# Revit family: 756-218-005 DN150-600
name_source: partatom
category: Pipe Accessories
units: mm (PartAtom-declared; Revit-internal decimal feet)

## family parameters
Always vertical = Yes
Cut with Voids When Loaded = No
Part Type = Valve - Breaks Into
Round Connector Dimension = Use Diameter
Shared = No
Work Plane-Based = No

## types (17) — shared parameters
1 = 1 mm  [stored 0.00328084 ft]
10 = 10 mm  [stored 0.0328084 ft]
15 = 15 mm  [stored 0.0492126 ft]
2 = 2 mm  [stored 0.00656168 ft]
20 = 20 mm  [stored 0.0656168 ft]
3 = 3 mm  [stored 0.00984252 ft]
40 = 40 mm  [stored 0.131234 ft]
82 = 84 mm
DN150_PN16 = 756-0150-2-14018014
DN200_PN10 = 756-0200-2-04018014
DN200_PN16 = 756-0200-2-14018014
DN250_PN10 = 756-0250-2-04018014
DN250_PN16 = 756-0250-2-14018014
DN300_PN10 = 756-0300-2-04018014
DN300_PN16 = 756-0300-2-14018014
DN350_PN10 = 756-0350-2-04018014
DN350_PN16 = 756-0350-2-14018014
DN400_PN10 = 756-0400-2-04018014
DN400_PN16 = 756-0400-2-14018014
DN450_PN10 = 756-0450-2-04018014
DN450_PN16 = 756-0450-2-14018014
DN500_PN10 = 756-0500-2-04018014
DN500_PN16 = 756-0500-2-14018014
DN600_PN10 = 756-0600-2-04018014
DN600_PN16 = 756-0600-2-14018014
Description_ = AVK DOUBLE ECC. BUTTERFLY VALVE, SHORT, PN10/16
Search_table = 756-218-005 DN150-600
URL_product_page = https://www.avkvalves.com
zero-valued in all types: Default Elevation

## per-type parameters (varying)
- DN150_PN16: Bore=75 mm; D=250 mm; D/2=125 mm; DN=150 mm; Disk_T=6 mm  [stored 0.019685 ft]; Disk_T1=6 mm  [stored 0.019685 ft]; FL_T=19 mm  [stored 0.062336 ft]; Fillet=8 mm  [stored 0.0262467 ft]; Gearbox_Sitting_OD=46 mm; Gearbox_Sitting_shaft=25 mm  [stored 0.082021 ft]; Gearbox_dim1=8 mm  [stored 0.0262467 ft]; Gearbox_od=44 mm; H2=201 mm; H2-H22=111 mm; H22=181 mm; Handwheel_dim2=5 mm  [stored 0.0164042 ft]; Handwheet_shaft=5 mm  [stored 0.0164042 ft]; L=140 mm; L/2=70 mm; L1=1 mm  [stored 0.00328084 ft]; L1+(L/2)=210 mm; L1+L/2=71 mm; L2=7 mm  [stored 0.0229659 ft]; L2+(L/2)=77 mm; Location1=28 mm  [stored 0.0918635 ft]; OD=143 mm; Raised_R=106 mm; Raised_dis=3 mm  [stored 0.00984252 ft]; Rib_H=157 mm; Rib_dim1=64 mm; Rib_dim2=45 mm; Thickness=5 mm  [stored 0.0164042 ft]; W1=155 mm; W11=147 mm; W2=263 mm; W2-W22=26 mm; W22=210 mm; W23=189 mm; W3=17 mm  [stored 0.0557743 ft]; W4=60 mm; W5=276 mm; W55=221 mm; disk_dim1=38 mm; disk_dim2=21 mm  [stored 0.0688976 ft]; disk_dim3=6 mm  [stored 0.019685 ft]; disk_dim4=7 mm  [stored 0.0229659 ft]; dist_Extr=14 mm  [stored 0.0459318 ft]; gearbox_dim2=18 mm  [stored 0.0590551 ft]; handwheel_dim1=3 mm  [stored 0.00984252 ft]; location=21 mm  [stored 0.0688976 ft]; raised_R1=110 mm; shaft_path=120 mm; total_dik_Dia=147 mm
- DN200_PN10: Bore=100 mm; D=250 mm; D/2=125 mm; DN=200 mm; Disk_T=10 mm  [stored 0.0328084 ft]; Disk_T1=6 mm  [stored 0.019685 ft]; FL_T=20 mm  [stored 0.0656168 ft]; Fillet=9 mm  [stored 0.0295276 ft]; Gearbox_Sitting_OD=50 mm; Gearbox_Sitting_shaft=28 mm  [stored 0.0918635 ft]; Gearbox_dim1=9 mm  [stored 0.0295276 ft]; Gearbox_od=48 mm; H2=227 mm; H2-H22=125 mm; H22=204 mm; Handwheel_dim2=6 mm  [stored 0.019685 ft]; Handwheet_shaft=5 mm  [stored 0.0164042 ft]; L=152 mm; L/2=76 mm; L1=15 mm  [stored 0.0492126 ft]; L1+(L/2)=230 mm; L1+L/2=91 mm; L2=25 mm  [stored 0.082021 ft]; L2+(L/2)=101 mm; Location1=31 mm; OD=170 mm; Raised_R=133 mm; Raised_dis=3 mm  [stored 0.00984252 ft]; Rib_H=187 mm; Rib_dim1=77 mm; Rib_dim2=54 mm; Thickness=5 mm  [stored 0.0164042 ft]; W1=182 mm; W11=173 mm; W2=287 mm; W2-W22=29 mm; W22=230 mm; W23=207 mm; W3=104 mm; W4=130 mm; W5=276 mm; W55=221 mm; disk_dim1=50 mm; disk_dim2=35 mm  [stored 0.114829 ft]; disk_dim3=11 mm  [stored 0.0360892 ft]; disk_dim4=12 mm  [stored 0.0393701 ft]; dist_Extr=15 mm  [stored 0.0492126 ft]; gearbox_dim2=20 mm  [stored 0.0656168 ft]; handwheel_dim1=4 mm  [stored 0.0131234 ft]; location=23 mm; raised_R1=138 mm; shaft_path=119 mm; total_dik_Dia=192 mm
- DN200_PN16: Bore=100 mm; D=250 mm; D/2=125 mm; DN=200 mm; Disk_T=10 mm  [stored 0.0328084 ft]; Disk_T1=7 mm  [stored 0.0229659 ft]; FL_T=20 mm  [stored 0.0656168 ft]; Fillet=9 mm  [stored 0.0295276 ft]; Gearbox_Sitting_OD=50 mm; Gearbox_Sitting_shaft=28 mm  [stored 0.0918635 ft]; Gearbox_dim1=9 mm  [stored 0.0295276 ft]; Gearbox_od=48 mm; H2=227 mm; H2-H22=125 mm; H22=204 mm; Handwheel_dim2=6 mm  [stored 0.019685 ft]; Handwheet_shaft=5 mm  [stored 0.0164042 ft]; L=152 mm; L/2=76 mm; L1=15 mm  [stored 0.0492126 ft]; L1+(L/2)=230 mm; L1+L/2=91 mm; L2=25 mm  [stored 0.082021 ft]; L2+(L/2)=101 mm; Location1=31 mm; OD=170 mm; Raised_R=133 mm; Raised_dis=3 mm  [stored 0.00984252 ft]; Rib_H=187 mm; Rib_dim1=77 mm; Rib_dim2=54 mm; Thickness=5 mm  [stored 0.0164042 ft]; W1=182 mm; W11=173 mm; W2=287 mm; W2-W22=29 mm; W22=230 mm; W23=207 mm; W3=104 mm; W4=130 mm; W5=276 mm; W55=221 mm; disk_dim1=50 mm; disk_dim2=35 mm  [stored 0.114829 ft]; disk_dim3=11 mm  [stored 0.0360892 ft]; disk_dim4=12 mm  [stored 0.0393701 ft]; dist_Extr=15 mm  [stored 0.0492126 ft]; gearbox_dim2=20 mm  [stored 0.0656168 ft]; handwheel_dim1=4 mm  [stored 0.0131234 ft]; location=23 mm; raised_R1=138 mm; shaft_path=119 mm; total_dik_Dia=192 mm
- DN250_PN10: Bore=125 mm; D=250 mm; D/2=125 mm; DN=250 mm; Disk_T=11 mm  [stored 0.0360892 ft]; Disk_T1=11 mm  [stored 0.0360892 ft]; FL_T=22 mm  [stored 0.0721785 ft]; Fillet=10 mm  [stored 0.0328084 ft]; Gearbox_Sitting_OD=54 mm; Gearbox_Sitting_shaft=30 mm  [stored 0.0984252 ft]; Gearbox_dim1=10 mm  [stored 0.0328084 ft]; Gearbox_od=52 mm; H2=261 mm; H2-H22=144 mm; H22=235 mm; Handwheel_dim2=6 mm  [stored 0.019685 ft]; Handwheet_shaft=5 mm  [stored 0.0164042 ft]; L=165 mm; L/2=83 mm; L1=34 mm  [stored 0.111549 ft]; L1+(L/2)=250 mm; L1+L/2=117 mm; L2=44 mm; L2+(L/2)=127 mm; Location1=33 mm  [stored 0.108268 ft]; OD=198 mm; Raised_R=160 mm; Raised_dis=3 mm  [stored 0.00984252 ft]; Rib_H=217 mm; Rib_dim1=89 mm; Rib_dim2=62 mm; Thickness=6 mm  [stored 0.019685 ft]; W1=215 mm; W11=204 mm; W2=321 mm; W2-W22=32 mm  [stored 0.104987 ft]; W22=257 mm; W23=231 mm; W3=162 mm; W4=181 mm; W5=276 mm; W55=221 mm; disk_dim1=63 mm; disk_dim2=39 mm; disk_dim3=12 mm  [stored 0.0393701 ft]; disk_dim4=13 mm  [stored 0.0426509 ft]; dist_Extr=17 mm  [stored 0.0557743 ft]; gearbox_dim2=22 mm  [stored 0.0721785 ft]; handwheel_dim1=4 mm  [stored 0.0131234 ft]; location=25 mm  [stored 0.082021 ft]; raised_R1=166 mm; shaft_path=119 mm; total_dik_Dia=243 mm
- DN250_PN16: Bore=125 mm; D=250 mm; D/2=125 mm; DN=250 mm; Disk_T=11 mm  [stored 0.0360892 ft]; Disk_T1=11 mm  [stored 0.0360892 ft]; FL_T=22 mm  [stored 0.0721785 ft]; Fillet=10 mm  [stored 0.0328084 ft]; Gearbox_Sitting_OD=54 mm; Gearbox_Sitting_shaft=30 mm  [stored 0.0984252 ft]; Gearbox_dim1=10 mm  [stored 0.0328084 ft]; Gearbox_od=52 mm; H2=261 mm; H2-H22=144 mm; H22=235 mm; Handwheel_dim2=6 mm  [stored 0.019685 ft]; Handwheet_shaft=5 mm  [stored 0.0164042 ft]; L=165 mm; L/2=83 mm; L1=34 mm  [stored 0.111549 ft]; L1+(L/2)=250 mm; L1+L/2=117 mm; L2=44 mm; L2+(L/2)=127 mm; Location1=33 mm  [stored 0.108268 ft]; OD=203 mm; Raised_R=160 mm; Raised_dis=3 mm  [stored 0.00984252 ft]; Rib_H=223 mm; Rib_dim1=91 mm; Rib_dim2=64 mm; Thickness=6 mm  [stored 0.019685 ft]; W1=215 mm; W11=204 mm; W2=321 mm; W2-W22=32 mm  [stored 0.104987 ft]; W22=257 mm; W23=231 mm; W3=162 mm; W4=181 mm; W5=276 mm; W55=221 mm; disk_dim1=63 mm; disk_dim2=39 mm; disk_dim3=12 mm  [stored 0.0393701 ft]; disk_dim4=13 mm  [stored 0.0426509 ft]; dist_Extr=17 mm  [stored 0.0557743 ft]; gearbox_dim2=22 mm  [stored 0.0721785 ft]; handwheel_dim1=4 mm  [stored 0.0131234 ft]; location=25 mm  [stored 0.082021 ft]; raised_R1=166 mm; shaft_path=119 mm; total_dik_Dia=243 mm
- DN300_PN10: Bore=150 mm; D=250 mm; D/2=125 mm; DN=300 mm; Disk_T=13 mm  [stored 0.0426509 ft]; Disk_T1=13 mm  [stored 0.0426509 ft]; FL_T=25 mm  [stored 0.082021 ft]; Fillet=11 mm  [stored 0.0360892 ft]; Gearbox_Sitting_OD=59 mm; Gearbox_Sitting_shaft=32 mm  [stored 0.104987 ft]; Gearbox_dim1=11 mm  [stored 0.0360892 ft]; Gearbox_od=56 mm; H2=292 mm; H2-H22=161 mm; H22=263 mm; Handwheel_dim2=6 mm  [stored 0.019685 ft]; Handwheet_shaft=6 mm  [stored 0.019685 ft]; L=178 mm; L/2=89 mm; L1=47 mm; L1+(L/2)=271 mm; L1+L/2=136 mm; L2=58 mm; L2+(L/2)=147 mm; Location1=36 mm  [stored 0.11811 ft]; OD=223 mm; Raised_R=185 mm; Raised_dis=4 mm  [stored 0.0131234 ft]; Rib_H=245 mm; Rib_dim1=100 mm; Rib_dim2=70 mm; Thickness=6 mm  [stored 0.019685 ft]; W1=242 mm; W11=230 mm; W2=352 mm; W2-W22=35 mm  [stored 0.114829 ft]; W22=282 mm; W23=253 mm; W3=209 mm; W4=227 mm; W5=276 mm; W55=221 mm; disk_dim1=75 mm; disk_dim2=44 mm; disk_dim3=13 mm  [stored 0.0426509 ft]; disk_dim4=15 mm  [stored 0.0492126 ft]; dist_Extr=18 mm  [stored 0.0590551 ft]; gearbox_dim2=23 mm; handwheel_dim1=4 mm  [stored 0.0131234 ft]; location=27 mm  [stored 0.0885827 ft]; raised_R1=192 mm; shaft_path=119 mm; total_dik_Dia=283 mm
- DN300_PN16: Bore=150 mm; D=400 mm; D/2=200 mm; DN=300 mm; Disk_T=13 mm  [stored 0.0426509 ft]; Disk_T1=13 mm  [stored 0.0426509 ft]; FL_T=25 mm  [stored 0.082021 ft]; Fillet=11 mm  [stored 0.0360892 ft]; Gearbox_Sitting_OD=59 mm; Gearbox_Sitting_shaft=32 mm  [stored 0.104987 ft]; Gearbox_dim1=11 mm  [stored 0.0360892 ft]; Gearbox_od=56 mm; H2=292 mm; H2-H22=161 mm; H22=263 mm; Handwheel_dim2=6 mm  [stored 0.019685 ft]; Handwheet_shaft=6 mm  [stored 0.019685 ft]; L=178 mm; L/2=89 mm; L1=47 mm; L1+(L/2)=271 mm; L1+L/2=136 mm; L2=58 mm; L2+(L/2)=147 mm; Location1=36 mm  [stored 0.11811 ft]; OD=230 mm; Raised_R=185 mm; Raised_dis=4 mm  [stored 0.0131234 ft]; Rib_H=253 mm; Rib_dim1=104 mm; Rib_dim2=72 mm; Thickness=6 mm  [stored 0.019685 ft]; W1=242 mm; W11=230 mm; W2=358 mm; W2-W22=36 mm  [stored 0.11811 ft]; W22=286 mm; W23=258 mm; W3=209 mm; W4=227 mm; W5=306 mm; W55=245 mm; disk_dim1=75 mm; disk_dim2=44 mm; disk_dim3=13 mm  [stored 0.0426509 ft]; disk_dim4=15 mm  [stored 0.0492126 ft]; dist_Extr=18 mm  [stored 0.0590551 ft]; gearbox_dim2=23 mm; handwheel_dim1=4 mm  [stored 0.0131234 ft]; location=27 mm  [stored 0.0885827 ft]; raised_R1=192 mm; shaft_path=194 mm; total_dik_Dia=283 mm
- DN350_PN10: Bore=175 mm; D=250 mm; D/2=125 mm; DN=350 mm; Disk_T=13 mm  [stored 0.0426509 ft]; Disk_T1=13 mm  [stored 0.0426509 ft]; FL_T=25 mm  [stored 0.082021 ft]; Fillet=11 mm  [stored 0.0360892 ft]; Gearbox_Sitting_OD=63 mm; Gearbox_Sitting_shaft=34 mm  [stored 0.111549 ft]; Gearbox_dim1=11 mm  [stored 0.0360892 ft]; Gearbox_od=60 mm; H2=318 mm; H2-H22=175 mm; H22=286 mm; Handwheel_dim2=7 mm  [stored 0.0229659 ft]; Handwheet_shaft=6 mm  [stored 0.019685 ft]; L=190 mm; L/2=95 mm; L1=68 mm; L1+(L/2)=310 mm; L1+L/2=163 mm; L2=74 mm; L2+(L/2)=169 mm; Location1=38 mm; OD=253 mm; Raised_R=215 mm; Raised_dis=4 mm  [stored 0.0131234 ft]; Rib_H=278 mm; Rib_dim1=114 mm; Rib_dim2=80 mm; Thickness=7 mm  [stored 0.0229659 ft]; W1=272 mm; W11=258 mm; W2=378 mm; W2-W22=38 mm; W22=302 mm; W23=272 mm; W3=266 mm; W4=274 mm; W5=276 mm; W55=221 mm; disk_dim1=88 mm; disk_dim2=44 mm; disk_dim3=13 mm  [stored 0.0426509 ft]; disk_dim4=15 mm  [stored 0.0492126 ft]; dist_Extr=19 mm  [stored 0.062336 ft]; gearbox_dim2=25 mm  [stored 0.082021 ft]; handwheel_dim1=4 mm  [stored 0.0131234 ft]; location=29 mm; raised_R1=223 mm; shaft_path=118 mm; total_dik_Dia=332 mm
- DN350_PN16: Bore=175 mm; D=400 mm; D/2=200 mm; DN=350 mm; Disk_T=14 mm  [stored 0.0459318 ft]; Disk_T1=14 mm  [stored 0.0459318 ft]; FL_T=27 mm  [stored 0.0885827 ft]; Fillet=11 mm  [stored 0.0360892 ft]; Gearbox_Sitting_OD=63 mm; Gearbox_Sitting_shaft=34 mm  [stored 0.111549 ft]; Gearbox_dim1=11 mm  [stored 0.0360892 ft]; Gearbox_od=60 mm; H2=318 mm; H2-H22=175 mm; H22=286 mm; Handwheel_dim2=7 mm  [stored 0.0229659 ft]; Handwheet_shaft=6 mm  [stored 0.019685 ft]; L=190 mm; L/2=95 mm; L1=68 mm; L1+(L/2)=310 mm; L1+L/2=163 mm; L2=74 mm; L2+(L/2)=169 mm; Location1=38 mm; OD=260 mm; Raised_R=215 mm; Raised_dis=4 mm  [stored 0.0131234 ft]; Rib_H=286 mm; Rib_dim1=117 mm; Rib_dim2=82 mm; Thickness=7 mm  [stored 0.0229659 ft]; W1=272 mm; W11=258 mm; W2=382 mm; W2-W22=38 mm; W22=306 mm; W23=275 mm; W3=266 mm; W4=274 mm; W5=306 mm; W55=245 mm; disk_dim1=88 mm; disk_dim2=47 mm; disk_dim3=14 mm  [stored 0.0459318 ft]; disk_dim4=16 mm  [stored 0.0524934 ft]; dist_Extr=19 mm  [stored 0.062336 ft]; gearbox_dim2=25 mm  [stored 0.082021 ft]; handwheel_dim1=4 mm  [stored 0.0131234 ft]; location=29 mm; raised_R1=223 mm; shaft_path=193 mm; total_dik_Dia=332 mm
- DN400_PN10: Bore=200 mm; D=400 mm; D/2=200 mm; DN=400 mm; Disk_T=13 mm  [stored 0.0426509 ft]; Disk_T1=13 mm  [stored 0.0426509 ft]; FL_T=25 mm  [stored 0.082021 ft]; Fillet=13 mm  [stored 0.0426509 ft]; Gearbox_Sitting_OD=71 mm; Gearbox_Sitting_shaft=39 mm; Gearbox_dim1=12 mm  [stored 0.0393701 ft]; Gearbox_od=68 mm; H2=349 mm; H2-H22=192 mm; H22=314 mm; Handwheel_dim2=8 mm  [stored 0.0262467 ft]; Handwheet_shaft=7 mm  [stored 0.0229659 ft]; L=216 mm; L/2=108 mm; L1=81 mm; L1+(L/2)=345 mm; L1+L/2=189 mm; L2=87 mm; L2+(L/2)=195 mm; Location1=44 mm; OD=283 mm; Raised_R=240 mm; Raised_dis=4 mm  [stored 0.0131234 ft]; Rib_H=311 mm; Rib_dim1=127 mm; Rib_dim2=89 mm; Thickness=8 mm  [stored 0.0262467 ft]; W1=302 mm; W11=287 mm; W2=413 mm; W2-W22=41 mm; W22=330 mm; W23=297 mm; W3=313 mm; W4=320 mm; W5=306 mm; W55=245 mm; disk_dim1=100 mm; disk_dim2=44 mm; disk_dim3=13 mm  [stored 0.0426509 ft]; disk_dim4=15 mm  [stored 0.0492126 ft]; dist_Extr=22 mm  [stored 0.0721785 ft]; gearbox_dim2=29 mm; handwheel_dim1=5 mm  [stored 0.0164042 ft]; location=32 mm  [stored 0.104987 ft]; raised_R1=250 mm; shaft_path=192 mm; total_dik_Dia=384 mm
- DN400_PN16: Bore=200 mm; D=400 mm; D/2=200 mm; DN=400 mm; Disk_T=14 mm  [stored 0.0459318 ft]; Disk_T1=14 mm  [stored 0.0459318 ft]; FL_T=28 mm  [stored 0.0918635 ft]; Fillet=13 mm  [stored 0.0426509 ft]; Gearbox_Sitting_OD=71 mm; Gearbox_Sitting_shaft=39 mm; Gearbox_dim1=12 mm  [stored 0.0393701 ft]; Gearbox_od=68 mm; H2=349 mm; H2-H22=192 mm; H22=314 mm; Handwheel_dim2=8 mm  [stored 0.0262467 ft]; Handwheet_shaft=7 mm  [stored 0.0229659 ft]; L=216 mm; L/2=108 mm; L1=81 mm; L1+(L/2)=345 mm; L1+L/2=189 mm; L2=87 mm; L2+(L/2)=195 mm; Location1=44 mm; OD=290 mm; Raised_R=240 mm; Raised_dis=4 mm  [stored 0.0131234 ft]; Rib_H=319 mm; Rib_dim1=131 mm; Rib_dim2=91 mm; Thickness=8 mm  [stored 0.0262467 ft]; W1=302 mm; W11=287 mm; W2=413 mm; W2-W22=41 mm; W22=330 mm; W23=297 mm; W3=313 mm; W4=320 mm; W5=306 mm; W55=245 mm; disk_dim1=100 mm; disk_dim2=49 mm; disk_dim3=15 mm  [stored 0.0492126 ft]; disk_dim4=17 mm  [stored 0.0557743 ft]; dist_Extr=22 mm  [stored 0.0721785 ft]; gearbox_dim2=29 mm; handwheel_dim1=5 mm  [stored 0.0164042 ft]; location=32 mm  [stored 0.104987 ft]; raised_R1=250 mm; shaft_path=192 mm; total_dik_Dia=384 mm
- DN450_PN10: Bore=225 mm; D=400 mm; D/2=200 mm; DN=450 mm; Disk_T=13 mm  [stored 0.0426509 ft]; Disk_T1=13 mm  [stored 0.0426509 ft]; FL_T=26 mm; Fillet=13 mm  [stored 0.0426509 ft]; Gearbox_Sitting_OD=73 mm; Gearbox_Sitting_shaft=40 mm  [stored 0.131234 ft]; Gearbox_dim1=14 mm  [stored 0.0459318 ft]; Gearbox_od=70 mm; H2=390 mm; H2-H22=215 mm; H22=351 mm; Handwheel_dim2=8 mm  [stored 0.0262467 ft]; Handwheet_shaft=7 mm  [stored 0.0229659 ft]; L=222 mm; L/2=111 mm; L1=102 mm; L1+(L/2)=378 mm; L1+L/2=213 mm; L2=108 mm; L2+(L/2)=219 mm; Location1=45 mm; OD=308 mm; Raised_R=265 mm; Raised_dis=4 mm  [stored 0.0131234 ft]; Rib_H=338 mm; Rib_dim1=138 mm; Rib_dim2=97 mm; Thickness=8 mm  [stored 0.0262467 ft]; W1=332 mm; W11=315 mm; W2=451 mm; W2-W22=45 mm; W22=361 mm; W23=325 mm; W3=365 mm; W4=374 mm; W5=306 mm; W55=245 mm; disk_dim1=113 mm; disk_dim2=46 mm; disk_dim3=14 mm  [stored 0.0459318 ft]; disk_dim4=16 mm  [stored 0.0524934 ft]; dist_Extr=22 mm  [stored 0.0721785 ft]; gearbox_dim2=29 mm; handwheel_dim1=5 mm  [stored 0.0164042 ft]; location=33 mm  [stored 0.108268 ft]; raised_R1=276 mm; shaft_path=192 mm; total_dik_Dia=432 mm
- DN450_PN16: Bore=225 mm; D=500 mm; D/2=250 mm; DN=450 mm; Disk_T=15 mm  [stored 0.0492126 ft]; Disk_T1=15 mm  [stored 0.0492126 ft]; FL_T=30 mm  [stored 0.0984252 ft]; Fillet=13 mm  [stored 0.0426509 ft]; Gearbox_Sitting_OD=73 mm; Gearbox_Sitting_shaft=40 mm  [stored 0.131234 ft]; Gearbox_dim1=14 mm  [stored 0.0459318 ft]; Gearbox_od=70 mm; H2=390 mm; H2-H22=215 mm; H22=351 mm; Handwheel_dim2=8 mm  [stored 0.0262467 ft]; Handwheet_shaft=7 mm  [stored 0.0229659 ft]; L=222 mm; L/2=111 mm; L1=102 mm; L1+(L/2)=378 mm; L1+L/2=213 mm; L2=108 mm; L2+(L/2)=219 mm; Location1=45 mm; OD=320 mm; Raised_R=274 mm; Raised_dis=4 mm  [stored 0.0131234 ft]; Rib_H=352 mm; Rib_dim1=144 mm; Rib_dim2=101 mm; Thickness=8 mm  [stored 0.0262467 ft]; W1=332 mm; W11=315 mm; W2=459 mm; W2-W22=46 mm; W22=367 mm; W23=330 mm; W3=365 mm; W4=374 mm; W5=416 mm; W55=333 mm; disk_dim1=113 mm; disk_dim2=53 mm; disk_dim3=16 mm  [stored 0.0524934 ft]; disk_dim4=18 mm  [stored 0.0590551 ft]; dist_Extr=22 mm  [stored 0.0721785 ft]; gearbox_dim2=29 mm; handwheel_dim1=5 mm  [stored 0.0164042 ft]; location=33 mm  [stored 0.108268 ft]; raised_R1=285 mm; shaft_path=242 mm; total_dik_Dia=432 mm
- DN500_PN10: Bore=250 mm; D=400 mm; D/2=200 mm; DN=500 mm; Disk_T=14 mm  [stored 0.0459318 ft]; Disk_T1=14 mm  [stored 0.0459318 ft]; FL_T=27 mm  [stored 0.0885827 ft]; Fillet=14 mm  [stored 0.0459318 ft]; Gearbox_Sitting_OD=76 mm; Gearbox_Sitting_shaft=42 mm; Gearbox_dim1=14 mm  [stored 0.0459318 ft]; Gearbox_od=72 mm; H2=417 mm; H2-H22=229 mm; H22=375 mm; Handwheel_dim2=8 mm  [stored 0.0262467 ft]; Handwheet_shaft=8 mm  [stored 0.0262467 ft]; L=229 mm; L/2=115 mm; L1=124 mm; L1+(L/2)=413 mm; L1+L/2=239 mm; L2=130 mm; L2+(L/2)=245 mm; Location1=46 mm; OD=335 mm; Raised_R=291 mm; Raised_dis=4 mm  [stored 0.0131234 ft]; Rib_H=369 mm; Rib_dim1=151 mm; Rib_dim2=106 mm; Thickness=8 mm  [stored 0.0262467 ft]; W1=338 mm; W11=321 mm; W2=479 mm; W2-W22=48 mm; W22=383 mm; W23=345 mm; W3=422 mm; W4=428 mm; W5=306 mm; W55=245 mm; disk_dim1=125 mm; disk_dim2=47 mm; disk_dim3=14 mm  [stored 0.0459318 ft]; disk_dim4=16 mm  [stored 0.0524934 ft]; dist_Extr=23 mm; gearbox_dim2=30 mm  [stored 0.0984252 ft]; handwheel_dim1=5 mm  [stored 0.0164042 ft]; location=34 mm  [stored 0.111549 ft]; raised_R1=303 mm; shaft_path=192 mm; total_dik_Dia=483 mm
- DN500_PN16: Bore=250 mm; D=500 mm; D/2=250 mm; DN=500 mm; Disk_T=16 mm  [stored 0.0524934 ft]; Disk_T1=16 mm  [stored 0.0524934 ft]; FL_T=32 mm  [stored 0.104987 ft]; Fillet=14 mm  [stored 0.0459318 ft]; Gearbox_Sitting_OD=76 mm; Gearbox_Sitting_shaft=42 mm; Gearbox_dim1=15 mm  [stored 0.0492126 ft]; Gearbox_od=72 mm; H2=427 mm; H2-H22=235 mm; H22=384 mm; Handwheel_dim2=8 mm  [stored 0.0262467 ft]; Handwheet_shaft=8 mm  [stored 0.0262467 ft]; L=229 mm; L/2=115 mm; L1=124 mm; L1+(L/2)=413 mm; L1+L/2=239 mm; L2=130 mm; L2+(L/2)=245 mm; Location1=46 mm; OD=358 mm; Raised_R=305 mm; Raised_dis=4 mm  [stored 0.0131234 ft]; Rib_H=393 mm; Rib_dim1=161 mm; Rib_dim2=113 mm; Thickness=8 mm  [stored 0.0262467 ft]; W1=370 mm; W11=352 mm; W2=496 mm; W2-W22=50 mm; W22=397 mm; W23=357 mm; W3=422 mm; W4=428 mm; W5=416 mm; W55=333 mm; disk_dim1=125 mm; disk_dim2=56 mm; disk_dim3=17 mm  [stored 0.0557743 ft]; disk_dim4=19 mm  [stored 0.062336 ft]; dist_Extr=23 mm; gearbox_dim2=30 mm  [stored 0.0984252 ft]; handwheel_dim1=5 mm  [stored 0.0164042 ft]; location=34 mm  [stored 0.111549 ft]; raised_R1=317 mm; shaft_path=242 mm; total_dik_Dia=483 mm
- DN600_PN10: Bore=300 mm; D=500 mm; D/2=250 mm; DN=600 mm; Disk_T=15 mm  [stored 0.0492126 ft]; Disk_T1=15 mm  [stored 0.0492126 ft]; FL_T=30 mm  [stored 0.0984252 ft]; Fillet=16 mm  [stored 0.0524934 ft]; Gearbox_Sitting_OD=88 mm; Gearbox_Sitting_shaft=48 mm; Gearbox_dim1=16 mm  [stored 0.0524934 ft]; Gearbox_od=84 mm; H2=476 mm; H2-H22=262 mm; H22=428 mm; Handwheel_dim2=10 mm  [stored 0.0328084 ft]; Handwheet_shaft=9 mm  [stored 0.0295276 ft]; L=267 mm; L/2=134 mm; L1=155 mm; L1+(L/2)=484 mm; L1+L/2=289 mm; L2=161 mm; L2+(L/2)=295 mm; Location1=54 mm; OD=390 mm; Raised_R=341 mm; Raised_dis=4 mm  [stored 0.0131234 ft]; Rib_H=429 mm; Rib_dim1=176 mm; Rib_dim2=123 mm; Thickness=10 mm  [stored 0.0328084 ft]; W1=393 mm; W11=373 mm; W2=546 mm; W2-W22=55 mm; W22=437 mm; W23=393 mm; W3=512 mm; W4=518 mm; W5=416 mm; W55=333 mm; disk_dim1=150 mm; disk_dim2=53 mm; disk_dim3=16 mm  [stored 0.0524934 ft]; disk_dim4=18 mm  [stored 0.0590551 ft]; dist_Extr=27 mm  [stored 0.0885827 ft]; gearbox_dim2=35 mm  [stored 0.114829 ft]; handwheel_dim1=6 mm  [stored 0.019685 ft]; location=40 mm  [stored 0.131234 ft]; raised_R1=355 mm; shaft_path=240 mm; total_dik_Dia=583 mm
- DN600_PN16: Bore=300 mm; D=600 mm; D/2=300 mm; DN=600 mm; Disk_T=18 mm  [stored 0.0590551 ft]; Disk_T1=18 mm  [stored 0.0590551 ft]; FL_T=36 mm  [stored 0.11811 ft]; Fillet=16 mm  [stored 0.0524934 ft]; Gearbox_Sitting_OD=88 mm; Gearbox_Sitting_shaft=48 mm; Gearbox_dim1=18 mm  [stored 0.0590551 ft]; Gearbox_od=84 mm; H2=502 mm; H2-H22=276 mm; H22=452 mm; Handwheel_dim2=10 mm  [stored 0.0328084 ft]; Handwheet_shaft=9 mm  [stored 0.0295276 ft]; L=267 mm; L/2=134 mm; L1=155 mm; L1+(L/2)=484 mm; L1+L/2=289 mm; L2=161 mm; L2+(L/2)=295 mm; Location1=54 mm; OD=420 mm; Raised_R=360 mm; Raised_dis=4 mm  [stored 0.0131234 ft]; Rib_H=462 mm; Rib_dim1=189 mm; Rib_dim2=132 mm; Thickness=10 mm  [stored 0.0328084 ft]; W1=435 mm; W11=413 mm; W2=587 mm; W2-W22=59 mm; W22=470 mm; W23=423 mm; W3=512 mm; W4=518 mm; W5=461 mm; W55=369 mm; disk_dim1=150 mm; disk_dim2=63 mm; disk_dim3=19 mm  [stored 0.062336 ft]; disk_dim4=22 mm  [stored 0.0721785 ft]; dist_Extr=27 mm  [stored 0.0885827 ft]; gearbox_dim2=35 mm  [stored 0.114829 ft]; handwheel_dim1=6 mm  [stored 0.019685 ft]; location=40 mm  [stored 0.131234 ft]; raised_R1=374 mm; shaft_path=290 mm; total_dik_Dia=583 mm

note: [stored X ft] marks values corroborated as IEEE doubles in the binary element streams (Revit-internal decimal feet)

## geometry (parser evidence)
native form markers: Sweep x5
no freeform markers — native parametric forms only
